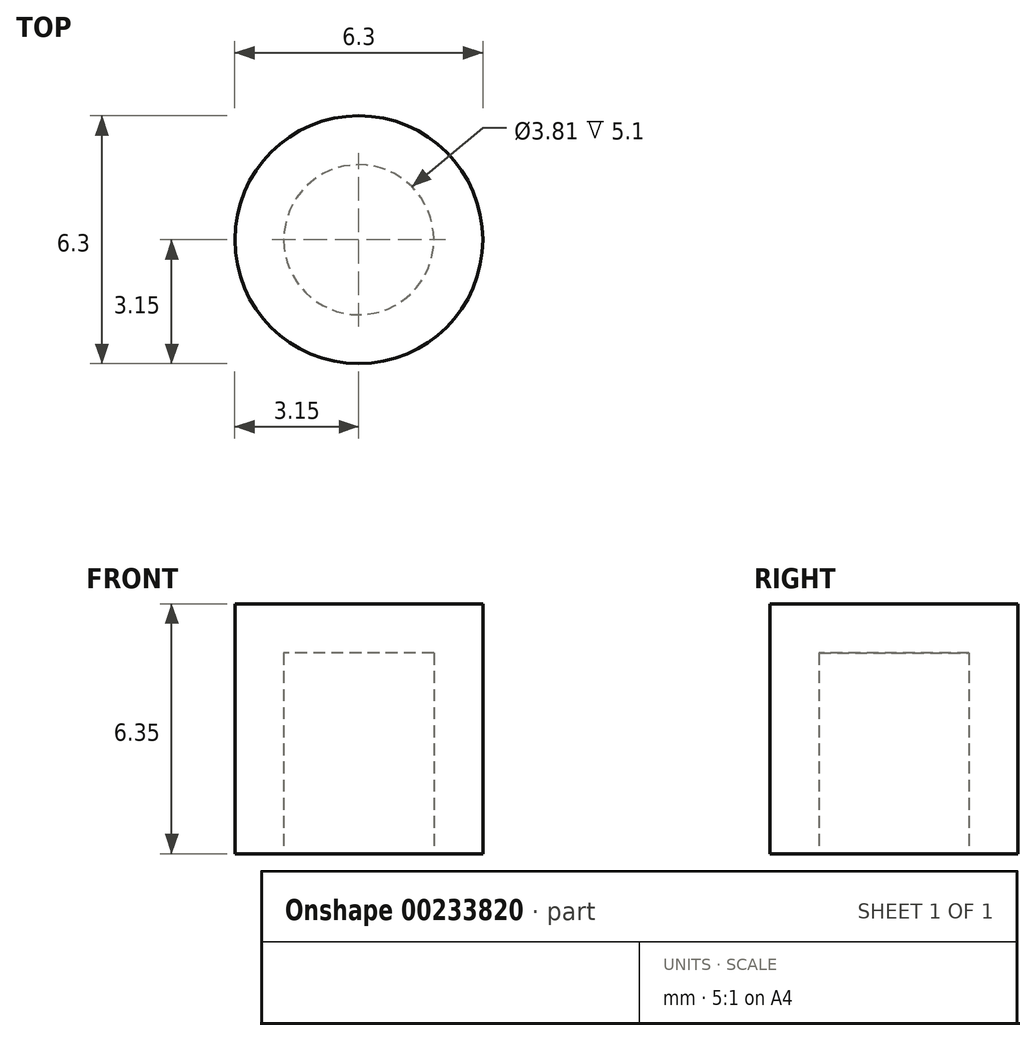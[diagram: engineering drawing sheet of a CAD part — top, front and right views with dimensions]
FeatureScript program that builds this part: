
annotation { "Feature Type Name" : "Feature", "Feature Type Description" : "" }
export const myFeature = defineFeature(function(context is Context, id is Id, definition is map)
    precondition{}
    {
        {
            var Q0;
            Q0=qCreatedBy(makeId("Top.planeOp"),FACE);
            var sketch = newSketch(context, id + "F0", { "sketchPlane" : qUnion([Q0])});
            skCircle(sketch, "E0", {"center": v(0, 0) * mm, "radius": 1.9 * mm});
            skCircle(sketch, "E1", {"center": v(0, 0) * mm, "radius": 3.15 * mm});
            skSolve(sketch);
        }
        {
            var Q0;
            Q0 = qSketchRegion(id + "F0", true);
            extrude(context, id + "F1", {"entities" : qUnion([Q0]), "depth" : 1.78 * mm});
        }
        {
            var Q0;
            Q0 = qSketchRegion(id + "F0", true);
            extrude(context, id + "F2", {"entities" : qUnion([Q0]), "operationType" : NewBodyOperationType.ADD, "depth" : 6.35 * mm});
        }
        {
            var Q0;
            Q0=makeQuery(id+"F2.opExtrude","CAP_FACE",FACE,{"disambiguationData":[OSD([sQuery(id+"F0.wireOp",EDGE,"E0"),sQuery(id+"F0.wireOp",EDGE,"E1")])],"isStart":false});
            var sketch = newSketch(context, id + "F3", { "sketchPlane" : qUnion([Q0])});
            skCircle(sketch, "E2", {"center": v(0, 0) * mm, "radius": 3.07 * mm});
            skSolve(sketch);
        }
        {
            var Q0;
            Q0 = qSketchRegion(id + "F3", true);
            extrude(context, id + "F4", {"entities" : qUnion([Q0]), "operationType" : NewBodyOperationType.ADD, "oppositeDirection" : true, "depth" : 1.25 * mm});
        }
    });
